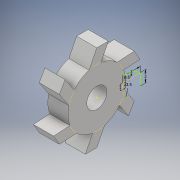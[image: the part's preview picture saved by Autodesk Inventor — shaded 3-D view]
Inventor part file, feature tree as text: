
AUTODESK INVENTOR PART (.ipt)
format: ipt  version: 2018 (Build 220112000, 112)  size: 290,304 bytes
history: native  units: mm
features: sketch x3, extrude x2, pattern_circular x1
ambient origin geometry x8: Origin, YZ Plane, XZ Plane, XY Plane, X Axis, Y Axis, Z Axis, Center Point
bodies: Solid1 (feature_tree)
feature tree (6):
  extrude  "Extrusion1"  Depth=10.0mm
  sketch  "Sketch2"  dims[d2=3.5mm d3=0.0mm d4=0.5mm]
  extrude  "Extrusion2"  Depth=3.5mm
  pattern_circular  "Circular Pattern1"  [2 undecoded]
  sketch  "Sketch1"  dims[d0=3.5mm d1=10.0mm]
  sketch  "Sketch3"  dims[d5=1.0mm d6=2.0mm d7=3.0mm d8=3.5mm d9=2.0mm d10=0.5mm d11=1.5mm d12=1.5mm d13=1.5mm d14=2.5mm d15=2.0mm d16=3.5mm d17=0.0mm d18=60.0mm d19=360.0deg]
note: 2 required parameter values undecoded (feature->parameter linkage not recoverable at this tier; creation-order binding heuristic only, values carry confidence <= 0.55)
